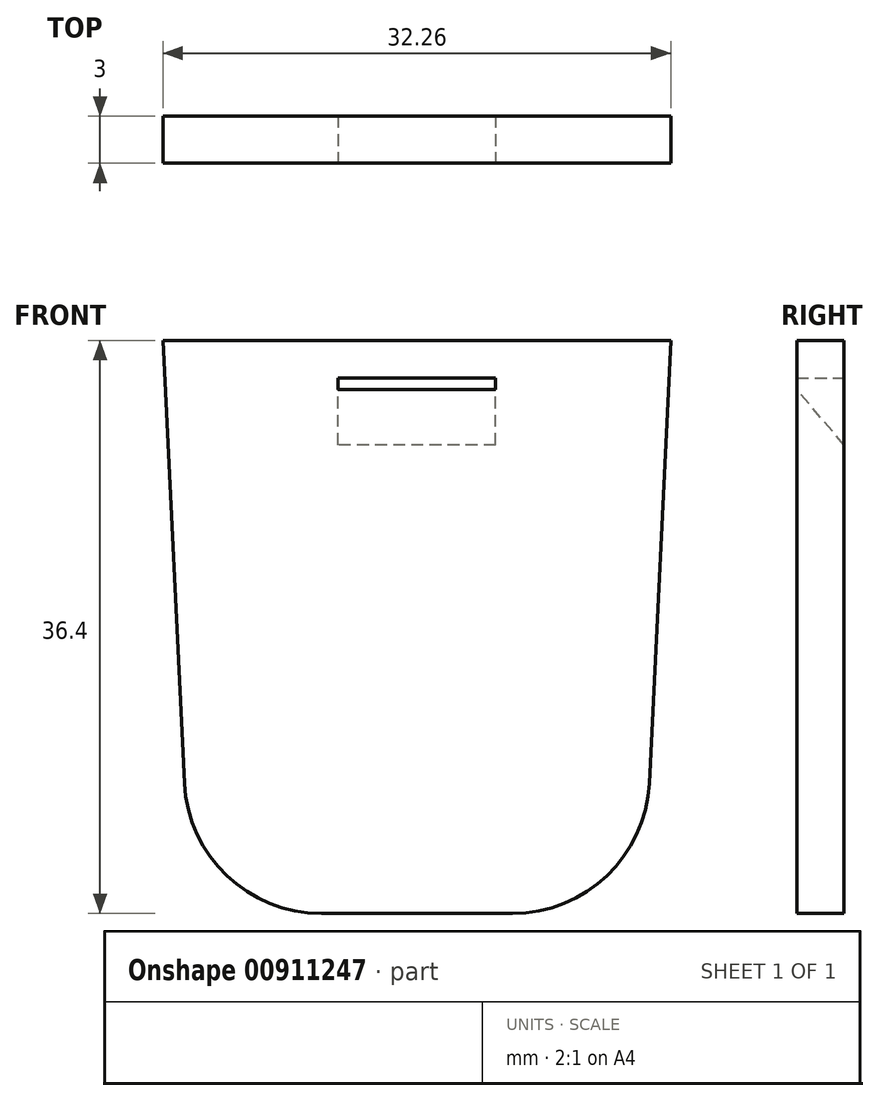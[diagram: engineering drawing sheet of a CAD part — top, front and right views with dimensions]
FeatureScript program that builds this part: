
annotation { "Feature Type Name" : "Feature", "Feature Type Description" : "" }
export const myFeature = defineFeature(function(context is Context, id is Id, definition is map)
    precondition{}
    {
        {
            var Q0;
            Q0=qCreatedBy(makeId("Front.planeOp"),FACE);
            var sketch = newSketch(context, id + "F0", { "sketchPlane" : qUnion([Q0])});
            skLineSegment(sketch, "E0.0", {"start": v(-14.76, -12.81) * mm, "end": v(-16.13, 15.3) * mm});
            skLineSegment(sketch, "E0.1", {"start": v(6.07, -21.1) * mm, "end": v(-6.07, -21.1) * mm});
            skArc(sketch, "E0.2", {"start": v(6.07, -21.1) * mm, "mid": v(12.07, -18.7) * mm, "end": v(14.76, -12.81) * mm});
            skArc(sketch, "E0.3", {"start": v(-14.76, -12.81) * mm, "mid": v(-12.07, -18.7) * mm, "end": v(-6.07, -21.1) * mm});
            skLineSegment(sketch, "E0.4", {"start": v(16.13, 15.3) * mm, "end": v(14.76, -12.81) * mm});
            skLineSegment(sketch, "E0.5", {"start": v(-16.13, 15.3) * mm, "end": v(16.13, 15.3) * mm});
            skSolve(sketch);
        }
        {
            var Q0;
            Q0 = qSketchRegion(id + "F0", true);
            extrude(context, id + "F1", {"entities" : qUnion([Q0]), "depth" : 3 * mm, "offsetDistance" : 25 * mm});
        }
        {
            var Q0;
            Q0=qCreatedBy(makeId("Right.planeOp"),FACE);
            var sketch = newSketch(context, id + "F2", { "sketchPlane" : qUnion([Q0])});
            skLineSegment(sketch, "E1.0", {"start": v(0.1, 8.56) * mm, "end": v(-3.63, 12.9) * mm});
            skLineSegment(sketch, "E1.1", {"start": v(0.1, 12.9) * mm, "end": v(0.1, 8.56) * mm});
            skLineSegment(sketch, "E1.2", {"start": v(-3.63, 12.9) * mm, "end": v(0.1, 12.9) * mm});
            skSolve(sketch);
        }
        {
            var Q0;
            Q0 = qSketchRegion(id + "F2", true);
            extrude(context, id + "F3", {"entities" : qUnion([Q0]), "operationType" : NewBodyOperationType.REMOVE, "endBound" : BoundingType.SYMMETRIC, "oppositeDirection" : true, "depth" : 10 * mm, "offsetDistance" : 25 * mm});
        }
    });
